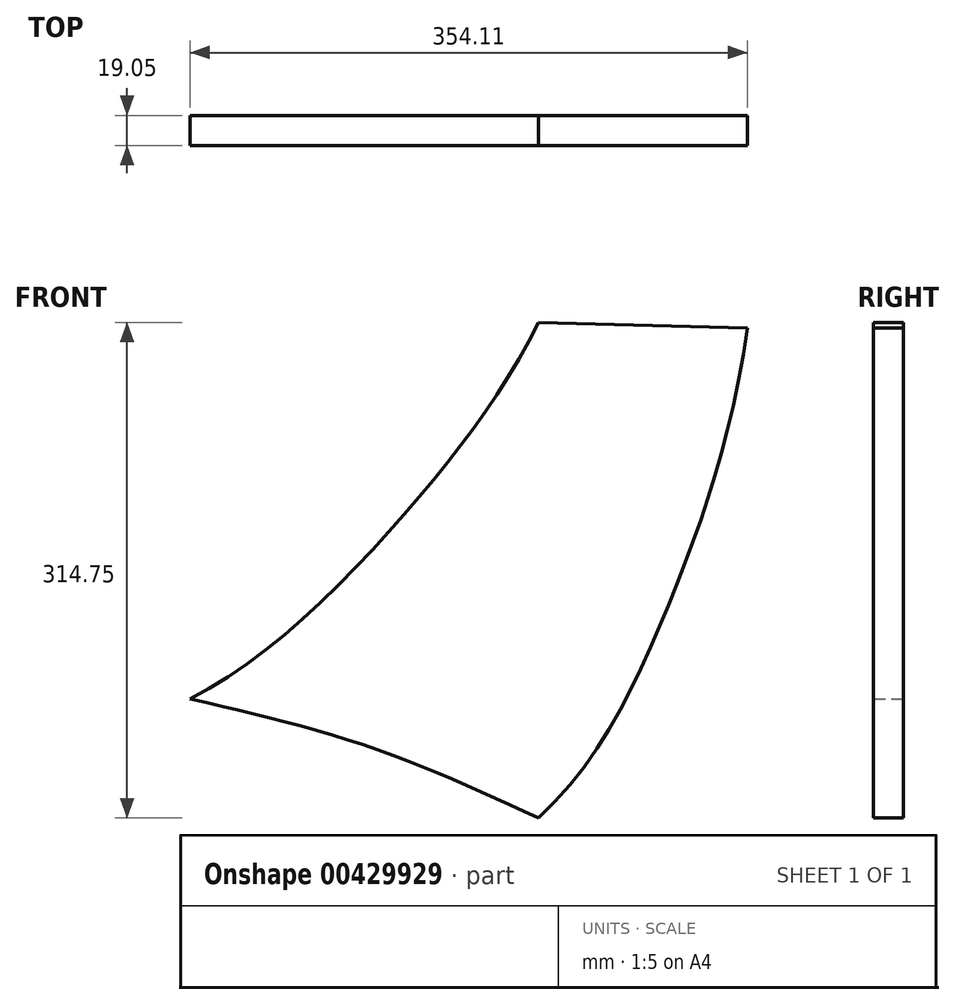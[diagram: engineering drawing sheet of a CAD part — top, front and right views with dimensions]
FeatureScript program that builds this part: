
annotation { "Feature Type Name" : "Feature", "Feature Type Description" : "" }
export const myFeature = defineFeature(function(context is Context, id is Id, definition is map)
    precondition{}
    {
        {
            var Q0;
            Q0=qCreatedBy(makeId("Front.planeOp"),FACE);
            var sketch = newSketch(context, id + "F0", { "sketchPlane" : qUnion([Q0])});
            skFitSpline(sketch, "E0", {"points": [v(-266.29, -285.49) * mm, v(-129.46, -167.48) * mm, v(-44.9, -46.52) * mm], "startDerivative": vector(278.43, 137.33) * mm, "endDerivative": vector(138.18, 273.59) * mm});
            skFitSpline(sketch, "E1", {"points": [v(-44.9, -361.27) * mm, v(38.5, -223.86) * mm, v(87.82, -50.04) * mm], "startDerivative": vector(244.97, 226.74) * mm, "endDerivative": vector(57.3, 396.82) * mm});
            skFitSpline(sketch, "E2", {"points": [v(-266.29, -285.49) * mm, v(-150.6, -316.64) * mm, v(-44.9, -361.27) * mm], "startDerivative": vector(232.75, -54.42) * mm, "endDerivative": vector(209.96, -97.3) * mm});
            skLineSegment(sketch, "E3", {"start": v(-44.9, -46.52) * mm, "end": v(87.82, -50.04) * mm});
            skSolve(sketch);
        }
        {
            var Q0;
            Q0 = qSketchRegion(id + "F0", true);
            extrude(context, id + "F1", {"entities" : qUnion([Q0]), "depth" : 19.05 * mm});
        }
    });
